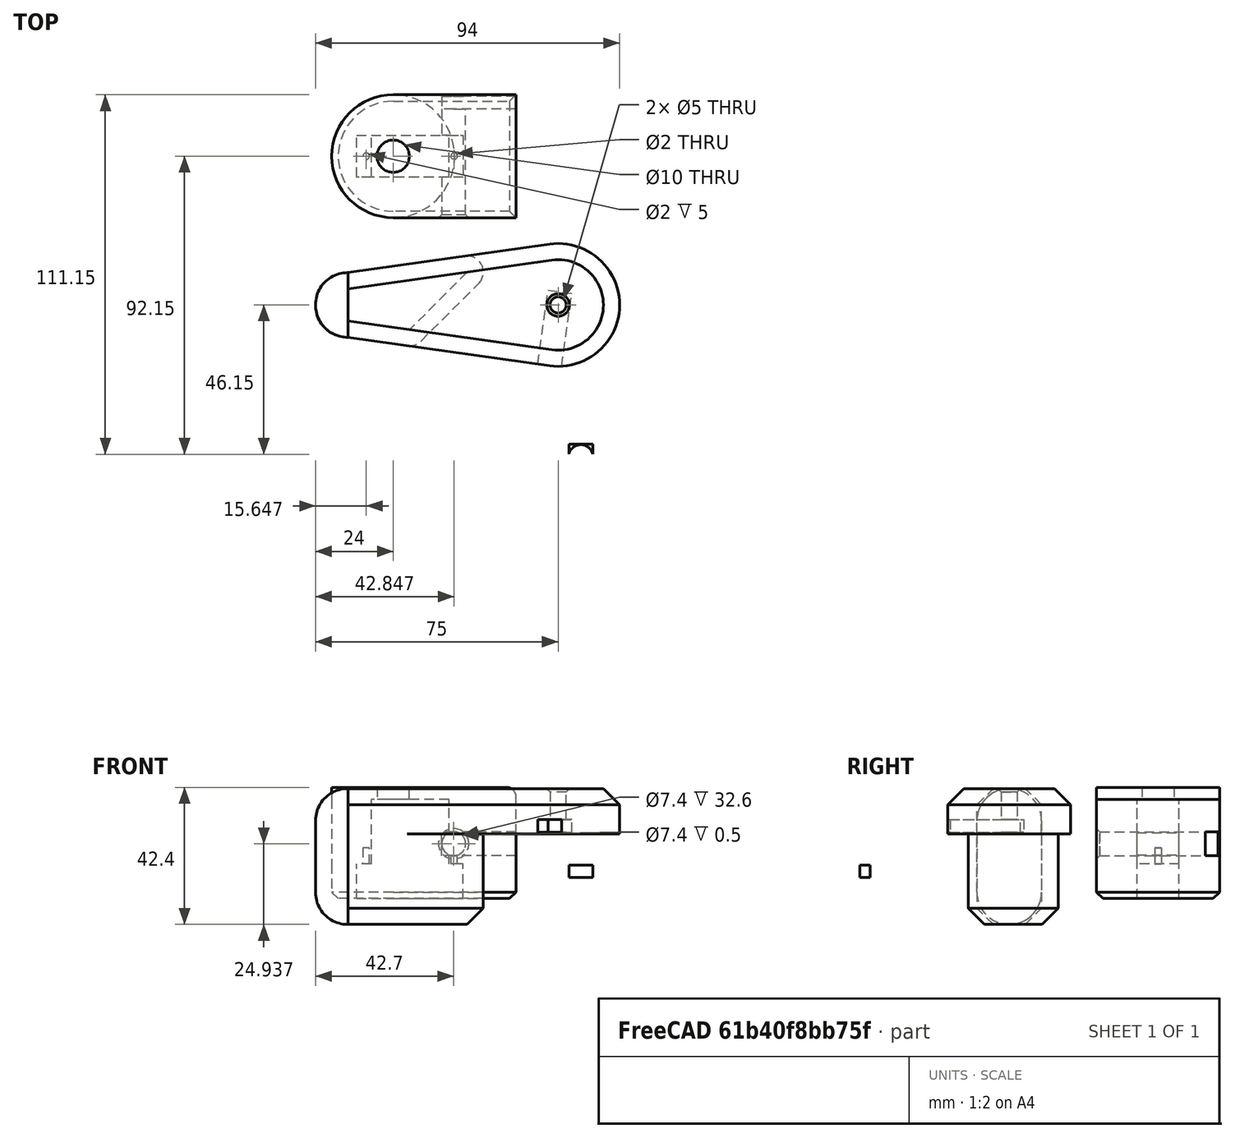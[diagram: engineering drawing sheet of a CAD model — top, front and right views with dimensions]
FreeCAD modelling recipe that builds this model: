
FCSTD DOCUMENT  (FreeCAD 0.17R13541 (Git))
Label: leftleg_decomposed
License: All rights reserved
LicenseURL: http://en.wikipedia.org/wiki/All_rights_reserved
objects: Sketcher::SketchObject×18, PartDesign::Pocket×11, PartDesign::Chamfer×11, PartDesign::Pad×7, PartDesign::Fillet×5, PartDesign::Body×3, PartDesign::ShapeBinder×1
note: 74 computed .brp shape members not serialized (recipe doc carries the construction recipe); baked Part::Feature solids carry a one-line shape summary decoded from their .brp

FEATURE [Sketcher::SketchObject] Sketch011
  MapMode = 5
  Support = -> [XY_Plane002]
  sketch-geometry (4):
    g0: ArcOfCircle CenterX=0 CenterY=0 CenterZ=0 NormalX=0 NormalY=0 NormalZ=1 AngleXU=0 Radius=19 StartAngle=1.5708 EndAngle=4.71239
    g1: ArcOfCircle CenterX=65 CenterY=0 CenterZ=0 NormalX=0 NormalY=0 NormalZ=1 AngleXU=0 Radius=19 StartAngle=4.71239 EndAngle=7.85398
    g2: LineSegment StartX=0 StartY=-19 StartZ=0 EndX=65 EndY=-19 EndZ=0
    g3: LineSegment StartX=0 StartY=19 StartZ=0 EndX=65 EndY=19 EndZ=0
  constraints (9):
    c: Coincident(g1,g2)
    c: Horizontal(g3)
    c: Horizontal(g2)
    c: Horizontal(g0,g1)
    c: DistanceX(g0,g1) = 65
    c: Tangent(g0,g3) = 1.5708
    c: Tangent(g0,g2) = -1.5708
    c: Tangent(g1,g3) = 1.5708
    c: Coincident(g0,g-1)
FEATURE [PartDesign::Pad] Pad008
  Length = 42
  Length2 = 100
  Profile = -> Sketch011
  Type = 0
FEATURE [Sketcher::SketchObject] Sketch012
  MapMode = 5
  Placement = pos=(0,0,42) rot=(0,0,1;0rad)
  Support = -> [Pad008]
  sketch-geometry (5):
    g0: ArcOfCircle CenterX=0 CenterY=0 CenterZ=0 NormalX=0 NormalY=0 NormalZ=1 AngleXU=0 Radius=19 StartAngle=1.5708 EndAngle=4.71239
    g1: LineSegment StartX=0 StartY=-19 StartZ=0 EndX=47.2 EndY=-19 EndZ=0
    g2: LineSegment StartX=0 StartY=19 StartZ=0 EndX=21.2711 EndY=19 EndZ=0
    g3: ArcOfCircle CenterX=21.2711 CenterY=14 CenterZ=0 NormalX=0 NormalY=0 NormalZ=1 AngleXU=0 Radius=5 StartAngle=1.5708 EndAngle=3.92699
    g4: LineSegment StartX=17.7355 StartY=10.4645 StartZ=0 EndX=47.2 EndY=-19 EndZ=0
  constraints (9):
    c: Coincident(g0,g-1)
    c: Horizontal(g2)
    c: Horizontal(g1)
    c: Tangent(g0,g2) = 1.5708
    c: Tangent(g0,g1) = -1.5708
    c: Tangent(g2,g3) = 1.5708
    c: Coincident(g1,g4)
    c: Angle(g4,g1) = 0.785398
    c: Tangent(g3,g4) = -1.5708
FEATURE [PartDesign::Pocket] Pocket003
  BaseFeature = -> Pad008
  Length = 14
  Length2 = 100
  Profile = -> Sketch012
  Type = 0
FEATURE [Sketcher::SketchObject] Sketch013
  MapMode = 5
  Placement = pos=(0,0,0) rot=(1,0,0;3.14159rad)
  Support = -> [Pocket003]
  sketch-geometry (4):
    g0: LineSegment StartX=-11.5912 StartY=6.6 StartZ=0 EndX=21.6088 EndY=6.6 EndZ=0
    g1: LineSegment StartX=21.6088 StartY=6.6 StartZ=0 EndX=21.6088 EndY=-6.6 EndZ=0
    g2: LineSegment StartX=21.6088 StartY=-6.6 StartZ=0 EndX=-11.5912 EndY=-6.6 EndZ=0
    g3: LineSegment StartX=-11.5912 StartY=-6.6 StartZ=0 EndX=-11.5912 EndY=6.6 EndZ=0
  constraints (11):
    c: Coincident(g0,g1)
    c: Coincident(g1,g2)
    c: Coincident(g2,g3)
    c: Coincident(g3,g0)
    c: Horizontal(g0)
    c: Horizontal(g2)
    c: Vertical(g1)
    c: Vertical(g3)
    c: DistanceY(g3,g3) = 13.2
    c: DistanceX(g0,g0) = 33.2
    c: DistanceY(g-1,g0) = 6.6
FEATURE [PartDesign::Pocket] Pocket004
  BaseFeature = -> Pocket003
  Length = 20.1
  Length2 = 100
  Profile = -> Sketch013
  Type = 0
FEATURE [Sketcher::SketchObject] Sketch014
  MapMode = 5
  Placement = pos=(0,0,20.1) rot=(1,0,0;3.14159rad)
  Support = -> [Pocket004]
  sketch-geometry (6):
    g0: LineSegment StartX=-6.69306 StartY=6.6 StartZ=0 EndX=17.1069 EndY=6.6 EndZ=0
    g1: LineSegment StartX=17.1069 StartY=6.6 StartZ=0 EndX=17.1069 EndY=-6.6 EndZ=0
    g2: LineSegment StartX=17.1069 StartY=-6.6 StartZ=0 EndX=-6.69306 EndY=-6.6 EndZ=0
    g3: LineSegment StartX=-6.69306 StartY=-6.6 StartZ=0 EndX=-6.69306 EndY=6.6 EndZ=0
    g4: Circle CenterX=-8.7165 CenterY=0 CenterZ=0 NormalX=0 NormalY=0 NormalZ=1 AngleXU=0 Radius=1
    g5: Circle CenterX=18.7883 CenterY=0 CenterZ=0 NormalX=0 NormalY=0 NormalZ=1 AngleXU=0 Radius=1
  constraints (15):
    c: Coincident(g0,g1)
    c: Coincident(g1,g2)
    c: Coincident(g2,g3)
    c: Coincident(g3,g0)
    c: Horizontal(g0)
    c: Horizontal(g2)
    c: Vertical(g1)
    c: Vertical(g3)
    c: DistanceX(g0,g0) = 23.8
    c: DistanceY(g3,g3) = 13.2
    c: DistanceY(g-1,g0) = 6.6
    c: Radius(g4) = 1
    c: Equal(g4,g5)
    c: PointOnObject(g4,g-1)
    c: PointOnObject(g5,g-1)
FEATURE [PartDesign::Pocket] Pocket005
  BaseFeature = -> Pocket004
  Length = 8
  Length2 = 100
  Profile = -> Sketch014
  Type = 0
FEATURE [PartDesign::Fillet] Fillet002
  Base = -> Pocket005 [Edge14]
  BaseFeature = -> Pocket005
  Radius = 5
FEATURE [PartDesign::Chamfer] Chamfer
  Base = -> Fillet002 [Edge9]
  BaseFeature = -> Fillet002
  Size = 5
FEATURE [Sketcher::SketchObject] Sketch015
  MapMode = 5
  Placement = pos=(0,0,0) rot=(1,0,0;3.14159rad)
  Support = -> [Chamfer]
  sketch-geometry (5):
    g0: LineSegment StartX=65 StartY=19 StartZ=0 EndX=28.7501 EndY=19 EndZ=0
    g1: LineSegment StartX=28.7501 StartY=19 StartZ=0 EndX=47.6229 EndY=0 EndZ=0
    g2: LineSegment StartX=47.6229 StartY=0 StartZ=0 EndX=28.4948 EndY=-19 EndZ=0
    g3: LineSegment StartX=28.4948 StartY=-19 StartZ=0 EndX=65 EndY=-19 EndZ=0
    g4: ArcOfCircle CenterX=65 CenterY=0 CenterZ=0 NormalX=0 NormalY=0 NormalZ=1 AngleXU=0 Radius=19 StartAngle=4.71239 EndAngle=7.85398
  constraints (14):
    c: Coincident(g0,g1)
    c: Coincident(g1,g2)
    c: Coincident(g2,g3)
    c: Coincident(g4,g3)
    c: Coincident(g0,g4)
    c: Horizontal(g0)
    c: Horizontal(g3)
    c: Tangent(g4,g0)
    c: Tangent(g3,g4)
    c: Perpendicular(g1,g2)
    c: Horizontal(g2,g4)
    c: PointOnObject(g4,g-1)
    c: Radius(g4) = 19
    c: DistanceX(g4) = 65
FEATURE [PartDesign::Pocket] Pocket006
  BaseFeature = -> Chamfer
  Length = 14
  Length2 = 100
  Profile = -> Sketch015
  Type = 0
FEATURE [PartDesign::Fillet] Fillet003
  Base = -> Pocket006 [Edge6,Edge33,Edge50]
  BaseFeature = -> Pocket006
  Radius = 5
FEATURE [PartDesign::Chamfer] Chamfer001
  Base = -> Fillet003 [Edge12]
  BaseFeature = -> Fillet003
  Size = 5
FEATURE [PartDesign::Chamfer] Chamfer002
  Base = -> Chamfer001 [Edge23]
  BaseFeature = -> Chamfer001
  Size = 1
FEATURE [PartDesign::Chamfer] Chamfer003
  Base = -> Chamfer002 [Edge31]
  BaseFeature = -> Chamfer002
  Size = 1
FEATURE [Sketcher::SketchObject] Sketch020
  ExternalGeometry = -> [Chamfer003]
  MapMode = 5
  Placement = pos=(0,-19,0) rot=(1,0,0;1.5708rad)
  Support = -> [Chamfer003]
  sketch-geometry (4):
    g0: LineSegment StartX=61.3 StartY=14.5 StartZ=0 EndX=68.7 EndY=14.5 EndZ=0
    g1: LineSegment StartX=68.7 StartY=14.5 StartZ=0 EndX=68.7 EndY=18.4 EndZ=0
    g2: LineSegment StartX=68.7 StartY=18.4 StartZ=0 EndX=61.3 EndY=18.4 EndZ=0
    g3: LineSegment StartX=61.3 StartY=18.4 StartZ=0 EndX=61.3 EndY=14.5 EndZ=0
  constraints (12):
    c: Coincident(g0,g1)
    c: Coincident(g1,g2)
    c: Coincident(g2,g3)
    c: Coincident(g3,g0)
    c: Horizontal(g0)
    c: Horizontal(g2)
    c: Vertical(g1)
    c: Vertical(g3)
    c: DistanceY(g3,g3) = 3.9
    c: DistanceX(g2,g2) = 7.4
    c: Distance(g0,g-3) = 0.5
    c: Distance(g2,g-4) = 3.7
FEATURE [PartDesign::Pocket] Pocket009
  BaseFeature = -> Chamfer003
  Length = 23
  Length2 = 100
  Profile = -> Sketch020
  Type = 0
FEATURE [Sketcher::SketchObject] Sketch021
  MapMode = 5
  Placement = pos=(0,0,42) rot=(0,0,1;0rad)
  Support = -> [Pocket009]
  sketch-geometry (1):
    g0: Circle CenterX=64.9965 CenterY=0 CenterZ=0 NormalX=0 NormalY=0 NormalZ=1 AngleXU=0 Radius=3.8
  constraints (3):
    c: PointOnObject(g0,g-1)
    c: Radius(g0) = 3.8
    c: DistanceX(g-1,g0) = 64.9965
FEATURE [PartDesign::Pocket] Pocket010
  BaseFeature = -> Pocket009
  Length = 23.1
  Length2 = 100
  Profile = -> Sketch021
  Type = 1
FEATURE [PartDesign::ShapeBinder] CopyPocket010
FEATURE [Sketcher::SketchObject] Sketch033
  MapMode = 5
  Placement = pos=(0,0,28) rot=(0,0,1;0rad)
  Support = -> [CopyPocket010]
  sketch-geometry (5):
    g0: ArcOfCircle CenterX=0 CenterY=0 CenterZ=0 NormalX=0 NormalY=0 NormalZ=1 AngleXU=0 Radius=19 StartAngle=4.57195 EndAngle=7.99442
    g1: LineSegment StartX=-2.65955 StartY=18.8129 StartZ=0 EndX=-65 EndY=10 EndZ=0
    g2: LineSegment StartX=-65 StartY=-10 StartZ=0 EndX=-2.65955 EndY=-18.8129 EndZ=0
    g3: LineSegment StartX=-65 StartY=10 StartZ=0 EndX=-65 EndY=-10 EndZ=0
    g4: LineSegment [constr] StartX=-65 StartY=0 StartZ=0 EndX=0 EndY=0 EndZ=0
  constraints (13):
    c: Vertical(g3)
    c: Coincident(g1,g3)
    c: Coincident(g2,g3)
    c: Coincident(g0,g-1)
    c: Radius(g0) = 19
    c: Tangent(g0,g1) = -1.5708
    c: Tangent(g0,g2) = -1.5708
    c: DistanceY(g-1,g1) = 10
    c: DistanceY(g3,g3) = 20
    c: Coincident(g0,g4)
    c: PointOnObject(g4,g-1)
    c: PointOnObject(g4,g3)
    c: DistanceX(g4,g4) = 65
FEATURE [PartDesign::Pad] Pad017
  Length = 14
  Length2 = 100
  Profile = -> Sketch033
  Type = 0
FEATURE [Sketcher::SketchObject] Sketch034
  ExternalGeometry = -> [Pad017]
  MapMode = 5
  Placement = pos=(0,0,28) rot=(1,0,0;3.14159rad)
  Support = -> [Pad017]
  sketch-geometry (4):
    g0: LineSegment StartX=-44.169 StartY=12.9448 StartZ=0 EndX=-14.0167 EndY=-17.2074 EndZ=0
    g1: LineSegment StartX=-44.169 StartY=12.9448 StartZ=0 EndX=-65 EndY=10 EndZ=0
    g2: LineSegment StartX=-65 StartY=10 StartZ=0 EndX=-65 EndY=-10 EndZ=0
    g3: LineSegment StartX=-65 StartY=-10 StartZ=0 EndX=-14.0167 EndY=-17.2074 EndZ=0
  constraints (10):
    c: Coincident(g1,g2)
    c: Coincident(g2,g3)
    c: Coincident(g0,g3)
    c: Coincident(g0,g1)
    c: Vertical(g2)
    c: DistanceY(g2,g2) = 20
    c: PointOnObject(g0,g-3)
    c: Coincident(g2,g-3)
    c: PointOnObject(g0,g-4)
    c: Angle(g0,g-1) = 0.785398
FEATURE [PartDesign::Pad] Pad018
  BaseFeature = -> Pad017
  Length = 28
  Length2 = 100
  Profile = -> Sketch034
  Type = 0
FEATURE [PartDesign::Fillet] Fillet006
  Base = -> Pad018 [Edge20,Edge16]
  BaseFeature = -> Pad018
  Radius = 5
FEATURE [Sketcher::SketchObject] Sketch035
  MapMode = 5
  Placement = pos=(-65,0,0) rot=(0.57735,-0.57735,-0.57735;2.0944rad)
  Support = -> [Fillet006]
  sketch-geometry (4):
    g0: ArcOfCircle CenterX=0 CenterY=32 CenterZ=0 NormalX=0 NormalY=0 NormalZ=1 AngleXU=0 Radius=10 StartAngle=6.28319 EndAngle=9.42478
    g1: ArcOfCircle CenterX=0 CenterY=10 CenterZ=0 NormalX=0 NormalY=0 NormalZ=1 AngleXU=0 Radius=10 StartAngle=3.14159 EndAngle=6.28319
    g2: LineSegment StartX=-10 StartY=32 StartZ=0 EndX=-10 EndY=10 EndZ=0
    g3: LineSegment StartX=10 StartY=10 StartZ=0 EndX=10 EndY=32 EndZ=0
  constraints (14):
    c: Coincident(g0,g3)
    c: Coincident(g0,g2)
    c: Coincident(g1,g2)
    c: Coincident(g1,g3)
    c: Vertical(g2)
    c: Vertical(g3)
    c: PointOnObject(g0,g-2)
    c: PointOnObject(g1,g-2)
    c: Radius(g0) = 10
    c: DistanceY(g1,g0) = 22
    c: Tangent(g0,g2)
    c: Tangent(g0,g3)
    c: Tangent(g2,g1)
    c: PointOnObject(g-1,g1)
FEATURE [PartDesign::Pad] Pad019
  BaseFeature = -> Fillet006
  Length = 10
  Length2 = 100
  Profile = -> Sketch035
  Type = 0
FEATURE [PartDesign::Fillet] Fillet007
  Base = -> Pad019 [Edge35]
  BaseFeature = -> Pad019
  Radius = 9.9
FEATURE [PartDesign::Chamfer] Chamfer004
  Base = -> Fillet007 [Edge42]
  BaseFeature = -> Fillet007
  Size = 5
FEATURE [Sketcher::SketchObject] Sketch036
  MapMode = 5
  Placement = pos=(-2.65955,-18.8129,0) rot=(0.995089,-0.069989,-0.069989;1.57572rad)
  sketch-geometry (4):
    g0: LineSegment StartX=-3.7 StartY=28.5 StartZ=0 EndX=3.7 EndY=28.5 EndZ=0
    g1: LineSegment StartX=3.7 StartY=28.5 StartZ=0 EndX=3.7 EndY=32.4 EndZ=0
    g2: LineSegment StartX=3.7 StartY=32.4 StartZ=0 EndX=-3.7 EndY=32.4 EndZ=0
    g3: LineSegment StartX=-3.7 StartY=32.4 StartZ=0 EndX=-3.7 EndY=28.5 EndZ=0
  constraints (11):
    c: Coincident(g0,g1)
    c: Coincident(g1,g2)
    c: Coincident(g2,g3)
    c: Coincident(g3,g0)
    c: Horizontal(g0)
    c: Horizontal(g2)
    c: Vertical(g1)
    c: Vertical(g3)
    c: DistanceY(g1,g1) = 3.9
    c: DistanceX(g2,g2) = 7.4
    c: DistanceX(g-1,g1) = 3.7
FEATURE [PartDesign::Chamfer] Chamfer005
  Base = -> Chamfer004 [Edge14]
  BaseFeature = -> Chamfer004
  Size = 5
FEATURE [PartDesign::Pocket] Pocket014
  BaseFeature = -> Chamfer005
  Length = 23
  Length2 = 100
  Profile = -> Sketch036
  Type = 0
FEATURE [Sketcher::SketchObject] Sketch037
  MapMode = 5
  Placement = pos=(0,0,28) rot=(1,0,0;3.14159rad)
  Support = -> [Pocket014]
  sketch-geometry (1):
    g0: Circle CenterX=0 CenterY=0 CenterZ=0 NormalX=0 NormalY=0 NormalZ=1 AngleXU=0 Radius=2.5
  constraints (2):
    c: Coincident(g0,g-1)
    c: Radius(g0) = 2.5
FEATURE [PartDesign::Pocket] Pocket015
  BaseFeature = -> Pocket014
  Length = 5
  Length2 = 100
  Profile = -> Sketch037
  Type = 1
FEATURE [PartDesign::Chamfer] Chamfer006
  Base = -> Pocket015 [Edge51]
  BaseFeature = -> Pocket015
  Size = 1
FEATURE [PartDesign::Body] Body005  label="molet"
  Group = -> [CopyPocket010,Sketch033,Pad017,Sketch034,Pad018,Fillet006,Sketch035,Pad019,Fillet007,Chamfer004,Sketch036,Chamfer005,Pocket014,Sketch037,Pocket015,Chamfer006]
  Origin = -> Origin005
  Tip = -> Chamfer006
FEATURE [PartDesign::Chamfer] Chamfer007
  Base = -> Pocket010 [Edge92]
  BaseFeature = -> Pocket010
  Size = 1
FEATURE [PartDesign::Body] Body002  label="upper_leg"
  Group = -> [Sketch011,Pad008,Sketch012,Pocket003,Sketch013,Pocket004,Sketch014,Pocket005,Fillet002,Chamfer,Sketch015,Pocket006,Fillet003,Chamfer001,Chamfer002,Chamfer003,Sketch020,Pocket009,Sketch021,Pocket010,Chamfer007]
  Origin = -> Origin002
  Placement = pos=(-58,-47,0) rot=(0,0,1;0rad)
  Tip = -> Chamfer007
FEATURE [Sketcher::SketchObject] Sketch038
  AttachmentOffset = pos=(65,0,0) rot=(0,0,1;0rad)
  MapMode = 5
  Placement = pos=(65,0,14) rot=(1,0,0;3.14159rad)
  sketch-geometry (8):
    g0: ArcOfCircle CenterX=0 CenterY=0 CenterZ=0 NormalX=0 NormalY=0 NormalZ=1 AngleXU=0 Radius=19 StartAngle=1.5708 EndAngle=4.71239
    g1: LineSegment StartX=2.30071e-07 StartY=19 StartZ=0 EndX=38 EndY=19 EndZ=0
    g2: LineSegment StartX=38 StartY=19 StartZ=0 EndX=38 EndY=-19 EndZ=0
    g3: LineSegment StartX=38 StartY=-19 StartZ=0 EndX=1.61106e-07 EndY=-19 EndZ=0
    g4: LineSegment StartX=-11.3413 StartY=6.51789 StartZ=0 EndX=21.6587 EndY=6.51789 EndZ=0
    g5: LineSegment StartX=21.6587 StartY=6.51789 StartZ=0 EndX=21.6587 EndY=-6.48211 EndZ=0
    g6: LineSegment StartX=21.6587 StartY=-6.48211 StartZ=0 EndX=-11.3413 EndY=-6.48211 EndZ=0
    g7: LineSegment StartX=-11.3413 StartY=-6.48211 StartZ=0 EndX=-11.3413 EndY=6.51789 EndZ=0
  constraints (22):
    c: Coincident(g1,g2)
    c: Coincident(g2,g3)
    c: Coincident(g0,g3)
    c: Coincident(g0,g1)
    c: Horizontal(g1)
    c: Horizontal(g3)
    c: Vertical(g2)
    c: Coincident(g0,g-1)
    c: DistanceX(g1,g1) = 38
    c: Tangent(g0,g1)
    c: Tangent(g0,g3)
    c: Radius(g0) = 19
    c: Coincident(g4,g5)
    c: Coincident(g5,g6)
    c: Coincident(g6,g7)
    c: Coincident(g7,g4)
    c: Horizontal(g4)
    c: Horizontal(g6)
    c: Vertical(g5)
    c: Vertical(g7)
    c: DistanceY(g7,g7) = 13
    c: DistanceX(g6,g6) = 33
FEATURE [PartDesign::Pad] Pad020
  Length = 10.7
  Length2 = 100
  Placement = pos=(65,0,14) rot=(1,0,0;3.14159rad)
  Profile = -> Sketch038
  Type = 0
FEATURE [Sketcher::SketchObject] Sketch039
  ExternalGeometry = -> [Pad020]
  MapMode = 5
  Placement = pos=(65,0,3.3) rot=(1,0,0;3.14159rad)
  Support = -> [Pad020]
  sketch-geometry (8):
    g0: ArcOfCircle CenterX=0 CenterY=0 CenterZ=0 NormalX=0 NormalY=0 NormalZ=1 AngleXU=0 Radius=19 StartAngle=1.5708 EndAngle=4.71239
    g1: LineSegment StartX=1.54623e-07 StartY=19 StartZ=0 EndX=38 EndY=19 EndZ=0
    g2: LineSegment StartX=38 StartY=19 StartZ=0 EndX=38 EndY=-19 EndZ=0
    g3: LineSegment StartX=38 StartY=-19 StartZ=0 EndX=3.21715e-05 EndY=-19 EndZ=0
    g4: LineSegment StartX=-6.77687 StartY=6.51789 StartZ=0 EndX=17.2231 EndY=6.51789 EndZ=0
    g5: LineSegment StartX=17.2231 StartY=6.51789 StartZ=0 EndX=17.2231 EndY=-6.48211 EndZ=0
    g6: LineSegment StartX=17.2231 StartY=-6.48211 StartZ=0 EndX=-6.77687 EndY=-6.48211 EndZ=0
    g7: LineSegment StartX=-6.77687 StartY=-6.48211 StartZ=0 EndX=-6.77687 EndY=6.51789 EndZ=0
  constraints (23):
    c: Coincident(g1,g2)
    c: Coincident(g2,g3)
    c: Coincident(g0,g3)
    c: Coincident(g0,g1)
    c: Horizontal(g3)
    c: Horizontal(g1)
    c: Vertical(g2)
    c: Coincident(g0,g-1)
    c: Radius(g0) = 19
    c: DistanceX(g1,g1) = 38
    c: Tangent(g0,g1)
    c: Tangent(g0,g3)
    c: Coincident(g4,g5)
    c: Coincident(g5,g6)
    c: Coincident(g6,g7)
    c: Coincident(g7,g4)
    c: Horizontal(g4)
    c: Horizontal(g6)
    c: Vertical(g5)
    c: Vertical(g7)
    c: PointOnObject(g5,g-4)
    c: PointOnObject(g4,g-3)
    c: DistanceX(g4,g4) = 24
FEATURE [PartDesign::Pad] Pad021
  BaseFeature = -> Pad020
  Length = 20
  Length2 = 100
  Placement = pos=(65,0,14) rot=(1,0,0;3.14159rad)
  Profile = -> Sketch039
  Type = 0
FEATURE [Sketcher::SketchObject] Sketch040
  MapMode = 5
  Placement = pos=(65,0,-16.7) rot=(1,0,0;3.14159rad)
  Support = -> [Pad021]
  sketch-geometry (5):
    g0: ArcOfCircle CenterX=0 CenterY=0 CenterZ=0 NormalX=0 NormalY=0 NormalZ=1 AngleXU=0 Radius=19 StartAngle=1.57079 EndAngle=4.71239
    g1: LineSegment StartX=3.80333e-05 StartY=19 StartZ=0 EndX=38 EndY=19 EndZ=0
    g2: LineSegment StartX=38 StartY=19 StartZ=0 EndX=38 EndY=-19 EndZ=0
    g3: LineSegment StartX=38 StartY=-19 StartZ=0 EndX=-1.65837e-07 EndY=-19 EndZ=0
    g4: Circle CenterX=0 CenterY=0 CenterZ=0 NormalX=0 NormalY=0 NormalZ=1 AngleXU=0 Radius=5
  constraints (14):
    c: Coincident(g1,g2)
    c: Coincident(g2,g3)
    c: Coincident(g0,g1)
    c: Coincident(g0,g3)
    c: Horizontal(g3)
    c: Horizontal(g1)
    c: Vertical(g2)
    c: Tangent(g0,g1)
    c: Tangent(g0,g3)
    c: Coincident(g0,g-1)
    c: Radius(g0) = 19
    c: DistanceX(g1,g1) = 38
    c: Coincident(g0,g4)
    c: Radius(g4) = 5
FEATURE [PartDesign::Pad] Pad022
  BaseFeature = -> Pad021
  Length = 3.7
  Length2 = 100
  Placement = pos=(65,0,14) rot=(1,0,0;3.14159rad)
  Profile = -> Sketch040
  Type = 0
FEATURE [PartDesign::Fillet] Fillet008
  Base = -> Pad022 [Edge57]
  BaseFeature = -> Pad022
  Placement = pos=(65,0,14) rot=(1,0,0;3.14159rad)
  Radius = 3
FEATURE [PartDesign::Chamfer] Chamfer008
  Base = -> Fillet008 [Edge44]
  BaseFeature = -> Fillet008
  Placement = pos=(65,0,14) rot=(1,0,0;3.14159rad)
  Size = 2
FEATURE [PartDesign::Chamfer] Chamfer009
  Base = -> Chamfer008 [Edge9]
  BaseFeature = -> Chamfer008
  Placement = pos=(65,0,14) rot=(1,0,0;3.14159rad)
  Size = 2
FEATURE [Sketcher::SketchObject] Sketch041
  ExternalGeometry = -> [Chamfer009]
  MapMode = 5
  Placement = pos=(103,0,14) rot=(0.57735,-0.57735,0.57735;4.18879rad)
  Support = -> [Chamfer009]
  sketch-geometry (4):
    g0: LineSegment StartX=14.6 StartY=20.6373 StartZ=0 EndX=18.5 EndY=20.6373 EndZ=0
    g1: LineSegment StartX=18.5 StartY=20.6373 StartZ=0 EndX=18.5 EndY=13.2373 EndZ=0
    g2: LineSegment StartX=18.5 StartY=13.2373 StartZ=0 EndX=14.6 EndY=13.2373 EndZ=0
    g3: LineSegment StartX=14.6 StartY=13.2373 StartZ=0 EndX=14.6 EndY=20.6373 EndZ=0
  constraints (11):
    c: Coincident(g0,g1)
    c: Coincident(g1,g2)
    c: Coincident(g2,g3)
    c: Coincident(g3,g0)
    c: Horizontal(g0)
    c: Horizontal(g2)
    c: Vertical(g1)
    c: Vertical(g3)
    c: DistanceX(g2,g2) = 3.9
    c: DistanceY(g3,g3) = 7.4
    c: Distance(g0,g-3) = 0.5
FEATURE [PartDesign::Pocket] Pocket016
  BaseFeature = -> Chamfer009
  Length = 23
  Length2 = 100
  Placement = pos=(65,0,14) rot=(1,0,0;3.14159rad)
  Profile = -> Sketch041
  Type = 0
FEATURE [Sketcher::SketchObject] Sketch042
  MapMode = 5
  Placement = pos=(65,0,3.3) rot=(0,0,1;0rad)
  Support = -> [Pocket016]
  sketch-geometry (2):
    g0: Circle CenterX=-8.35268 CenterY=0 CenterZ=0 NormalX=0 NormalY=0 NormalZ=1 AngleXU=0 Radius=1
    g1: Circle CenterX=18.8473 CenterY=0 CenterZ=0 NormalX=0 NormalY=0 NormalZ=1 AngleXU=0 Radius=1
  constraints (5):
    c: PointOnObject(g0,g-1)
    c: PointOnObject(g1,g-1)
    c: DistanceX(g0,g1) = 27.2
    c: Radius(g0) = 1
    c: Radius(g1) = 1
FEATURE [PartDesign::Pocket] Pocket017
  BaseFeature = -> Pocket016
  Length = 5
  Length2 = 100
  Placement = pos=(65,0,14) rot=(1,0,0;3.14159rad)
  Profile = -> Sketch042
  Type = 0
FEATURE [Sketcher::SketchObject] Sketch043
  ExternalGeometry = -> [Pocket017]
  MapMode = 5
  Placement = pos=(65,-19,14) rot=(0,0.707107,-0.707107;3.14159rad)
  Support = -> [Pocket017]
  sketch-geometry (1):
    g0: Circle CenterX=-18.7 CenterY=16.9373 CenterZ=0 NormalX=0 NormalY=0 NormalZ=1 AngleXU=0 Radius=3.7
  constraints (3):
    c: Radius(g0) = 3.7
    c: Tangent(g-4,g0)
    c: Tangent(g-3,g0)
FEATURE [PartDesign::Pocket] Pocket018
  BaseFeature = -> Pocket017
  Length = 5
  Length2 = 100
  Placement = pos=(65,0,14) rot=(1,0,0;3.14159rad)
  Profile = -> Sketch043
  Type = 1
FEATURE [PartDesign::Chamfer] Chamfer010
  Base = -> Pocket018 [Edge39]
  BaseFeature = -> Pocket018
  Placement = pos=(65,0,14) rot=(1,0,0;3.14159rad)
  Size = 1
FEATURE [PartDesign::Body] Body006  label="Hip"
  Group = -> [Sketch038,Pad020,Sketch039,Pad021,Sketch040,Pad022,Fillet008,Chamfer008,Chamfer009,Sketch041,Pocket016,Sketch042,Pocket017,Sketch043,Pocket018,Chamfer010]
  Origin = -> Origin006
  Placement = pos=(-116,46,22) rot=(1,0,0;3.14159rad)
  Tip = -> Chamfer010
